# Revit family: Sanitary_Wash-Basins_HIMACS_HIMACS-Bowl-CB-4232
name_source: partatom
category: Plumbing Fixtures
revit_build: Autodesk Revit 2018 (Build: 20190510_1515(x64)
units: mm (PartAtom-declared; Revit-internal decimal feet)

## family parameters
Cut with Voids When Loaded = No
Host = Face
OmniClass Number = 23.31.13.11
OmniClass Title = Single Sinks
Part Type = Normal
Room Calculation Point = No
Round Connector Dimension = Use Diameter
Shared = No

## types (1)
- HIMACS Bowl CB 4232
    Always visible = Yes
    BIMobject category = Wash Basins
    Default Elevation = 1219 mm
    Description = HIMACS Bowls offer superb ease of cleaning and a warm and pleasant feel, making them the ideal solution for creating the bathroom of your dreams. They are manufactured using a casting process and ideally suited for both flush mounting and installation into a bathroom vanity top.

Available in Alpine White S028.

With or without overflow. Under Mounted.

HIMACS is a solid surface material that can be moulded into any shape. It is widely used for architectural and interior applications, such as sculptural and high performance wall-cladding or kitchen, bathroom and furniture surfaces, in commercial, residential and public space projects. It is composed of acrylic, natural minerals and pigments that come together to provide a smooth, non-porous and visually seamless surface which meets the highest standards for quality, aesthetics, fabrication, functionality and hygiene – offering manifold advantages over conventional materials.

Visit himacs.eu for more information.
    Design country = Spain
    Diameter = 45 mm  [stored 0.147638 ft]
    Edition number = 1
    IFC Classification = Furnishing Element
    Main Material = HIMACS - Ceramic - Alpine White
    Manufacturer = Himacs
    Manufacturer country = Spain
    Manufacturer name = HIMACS
    Material main = Solid surface
    Material secondary = Natural Acrylic Stone
    Model = HIMACS Bowl CB 4232
    NBS Reference Code = 35-65-70-94
    NBS Reference Description = Wash Basin Systems
    Product Guid = 073b2364-3bcc-4250-bc9c-8a204af13c8c
    Product SKU = CB4232
    Product certification = http://himacs.eu
    Product data url = https://bimobject.com
    Product family = Sinks, Baby Baths & Bowls
    Product group = Bowls
    Product name = HIMACS Bowl CB 4232
    QR code = https://bimobject.com
    UNSPSC Code = 301815
    URL = https://himacs.eu
    Uniclass 1.4 Code = L7212
    Uniclass 1.4 Description = Washbasins
    Uniclass 2.0 Code = SS-35-65-70-94
    Uniclass 2.0 Description = Wash Basin Systems
    Weight Net (Kg) = 4,75

note: [stored X ft] marks values corroborated as IEEE doubles in the binary element streams (Revit-internal decimal feet)

## geometry (parser evidence)
native form markers: Sweep x3
no freeform markers — native parametric forms only
